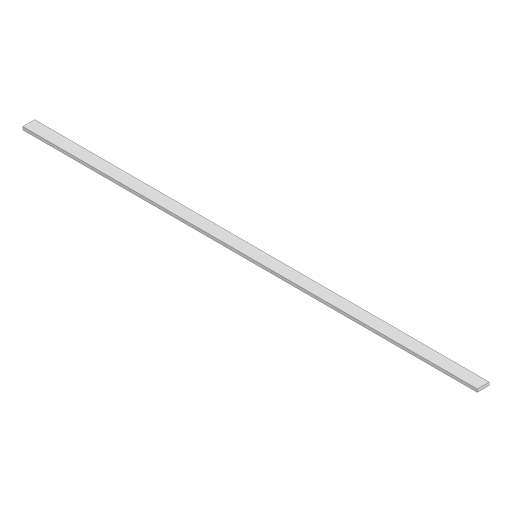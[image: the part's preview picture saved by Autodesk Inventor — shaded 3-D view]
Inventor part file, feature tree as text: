
AUTODESK INVENTOR PART (.ipt)
format: ipt  version: 2024 (Build 280153000, 153)  size: 82,432 bytes
history: native  units: in
note: dims shown in document units (in); Inventor stores cm internally (conversion verified against a paired STEP export)
features: extrude x1, sketch x1
ambient origin geometry x8: Origin, YZ Plane, XZ Plane, XY Plane, X Axis, Y Axis, Z Axis, Center Point
bodies: Solid1 (feature_tree)
feature tree (2):
  extrude  "Extrusion1"  Depth=10.315in
  sketch  "Sketch1"  dims[d0=2.5591in d1=10.315in d2=393.7008in d3=0.0in d4=0.0197in d5=0.0344in d6=0.0197in d7=0.0344in]
